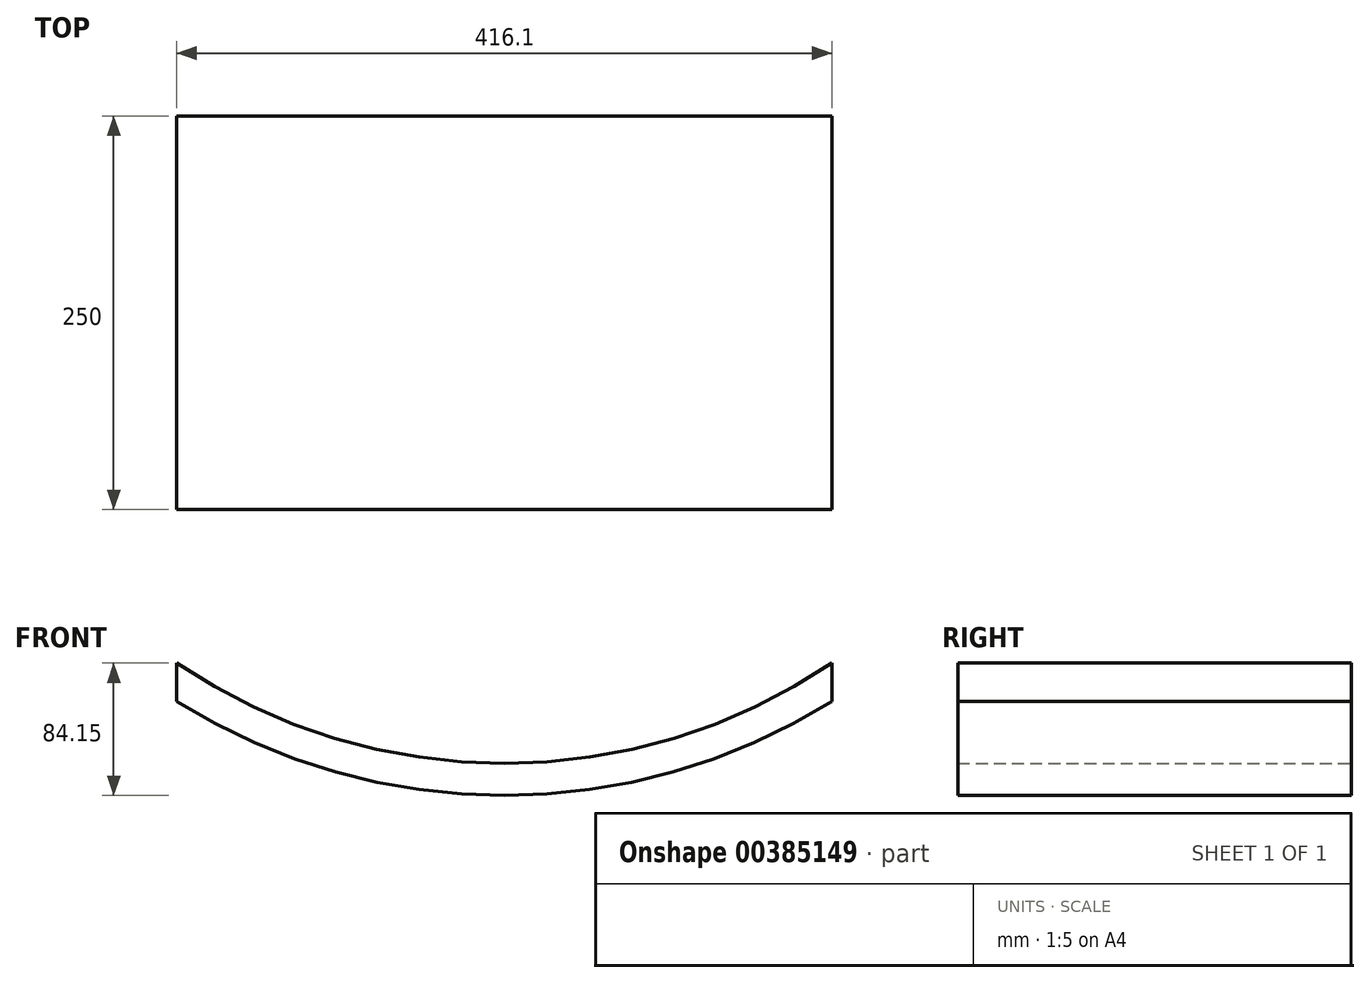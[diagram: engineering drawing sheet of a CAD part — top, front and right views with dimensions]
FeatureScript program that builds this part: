
annotation { "Feature Type Name" : "Feature", "Feature Type Description" : "" }
export const myFeature = defineFeature(function(context is Context, id is Id, definition is map)
    precondition{}
    {
        {
            var Q0;
            Q0=qCreatedBy(makeId("Front.planeOp"),FACE);
            var sketch = newSketch(context, id + "F0", { "sketchPlane" : qUnion([Q0])});
            skArc(sketch, "E0", {"start": v(-33.05, 109.24) * mm, "mid": v(175, 49.43) * mm, "end": v(383.05, 109.24) * mm});
            skArc(sketch, "E1.0", {"start": v(-33.05, 133.58) * mm, "mid": v(175, 69.83) * mm, "end": v(383.05, 133.58) * mm});
            skLineSegment(sketch, "E2", {"start": v(383.05, 109.24) * mm, "end": v(383.05, 133.58) * mm});
            skLineSegment(sketch, "E3", {"start": v(-33.05, 109.24) * mm, "end": v(-33.05, 133.58) * mm});
            skSolve(sketch);
        }
        {
            var Q0;
            Q0=makeQuery(id+"F0.imprint","IMPRINT",FACE,{"disambiguationData":[TD([[makeQuery(id+"F0.imprint","IMPRINT",EDGE,{"derivedFrom":sQuery(id+"F0.wireOp",EDGE,"E0")}),1.0]])]});
            extrude(context, id + "F1", {"entities" : qUnion([Q0]), "depth" : 250 * mm});
        }
    });
